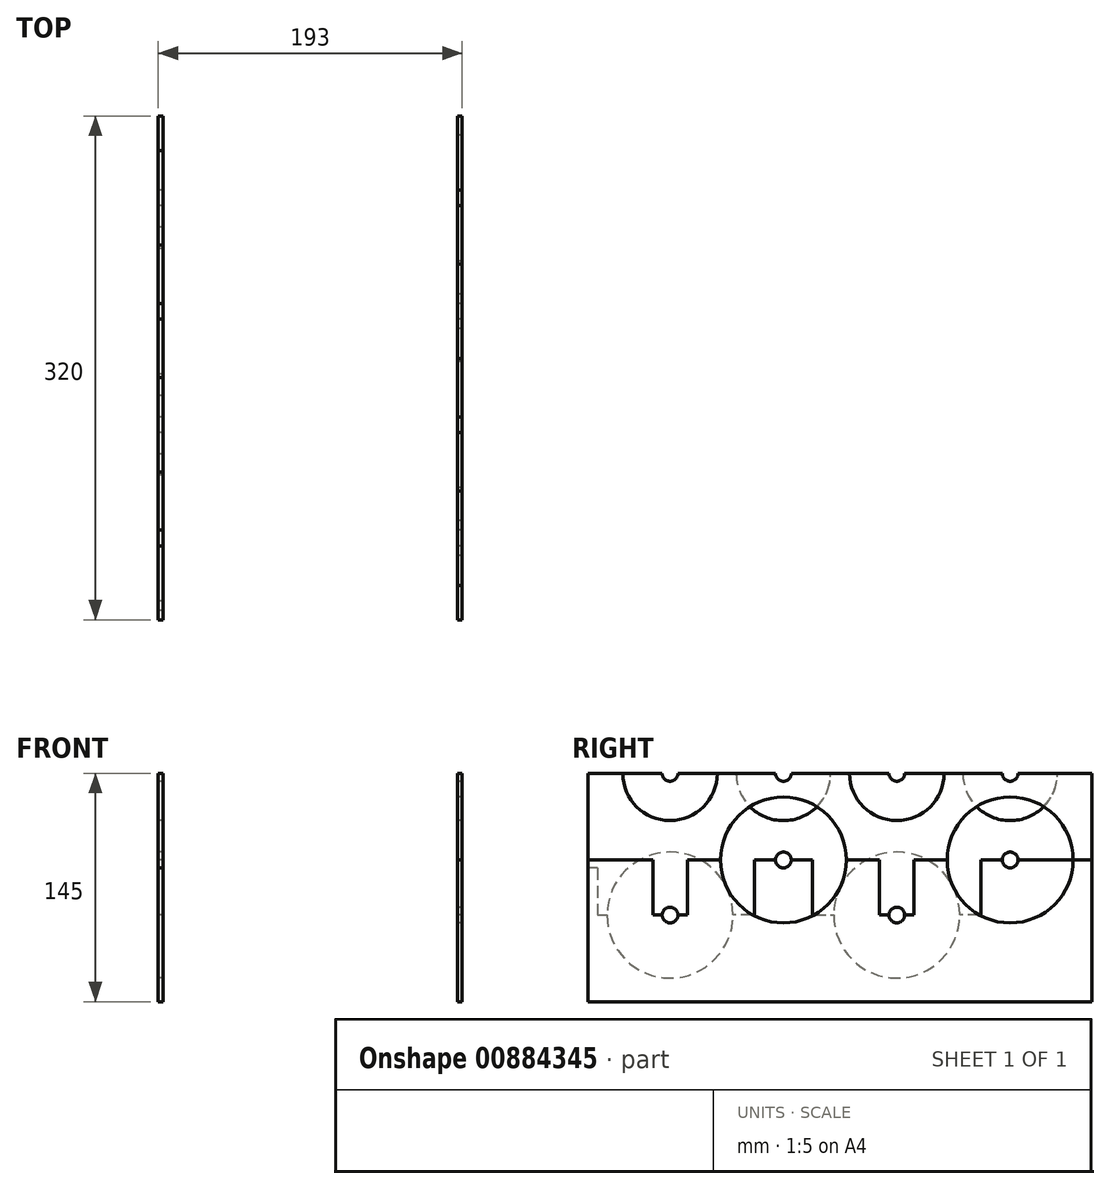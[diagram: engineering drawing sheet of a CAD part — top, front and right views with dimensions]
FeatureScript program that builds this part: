
annotation { "Feature Type Name" : "Feature", "Feature Type Description" : "" }
export const myFeature = defineFeature(function(context is Context, id is Id, definition is map)
    precondition{}
    {
        {
            var Q0;
            Q0=qCreatedBy(makeId("Right.planeOp"),FACE);
            var sketch = newSketch(context, id + "F0", { "sketchPlane" : qUnion([Q0])});
            skLineSegment(sketch, "E0.bottom", {"start": v(160, -42.5) * mm, "end": v(-160, -42.5) * mm});
            skLineSegment(sketch, "E0.right", {"start": v(-160, -42.5) * mm, "end": v(-160, 42.5) * mm});
            skPoint(sketch, "E0.middle", {"position": v(0, 0) * mm});
            skArc(sketch, "E1", {"start": v(-68, 12.5) * mm, "mid": v(-108, -27.5) * mm, "end": v(-148, 12.5) * mm});
            skArc(sketch, "E2", {"start": v(-4, 12.5) * mm, "mid": v(36, -27.5) * mm, "end": v(76, 12.5) * mm});
            skPoint(sketch, "E3", {"position": v(11.64, 12.5) * mm});
            skArc(sketch, "E4", {"start": v(113, 47.5) * mm, "mid": v(108, 42.5) * mm, "end": v(103, 47.5) * mm});
            skArc(sketch, "E5", {"start": v(-31, 47.5) * mm, "mid": v(-36, 42.5) * mm, "end": v(-41, 47.5) * mm});
            skLineSegment(sketch, "E6", {"start": v(-54.5, 47.5) * mm, "end": v(-41, 47.5) * mm});
            skLineSegment(sketch, "E7", {"start": v(89.5, 47.5) * mm, "end": v(103, 47.5) * mm});
            skLineSegment(sketch, "E8.trimOffspring", {"start": v(-31, 47.5) * mm, "end": v(-17.5, 47.5) * mm});
            skLineSegment(sketch, "E9.trimOffspring", {"start": v(113, 47.5) * mm, "end": v(160, 47.5) * mm});
            skLineSegment(sketch, "E10", {"start": v(160, -42.5) * mm, "end": v(160, 47.5) * mm});
            skLineSegment(sketch, "E11", {"start": v(-154, 42.5) * mm, "end": v(-160, 42.5) * mm});
            skLineSegment(sketch, "E12", {"start": v(-17.5, 47.5) * mm, "end": v(-17.5, 12.5) * mm});
            skLineSegment(sketch, "E13", {"start": v(-17.5, 12.5) * mm, "end": v(-4, 12.5) * mm});
            skLineSegment(sketch, "E14", {"start": v(89.5, 47.5) * mm, "end": v(89.5, 12.5) * mm});
            skLineSegment(sketch, "E15", {"start": v(89.5, 12.5) * mm, "end": v(76, 12.5) * mm});
            skLineSegment(sketch, "E16", {"start": v(-54.5, 47.5) * mm, "end": v(-54.5, 12.5) * mm});
            skLineSegment(sketch, "E17", {"start": v(-54.5, 12.5) * mm, "end": v(-68, 12.5) * mm});
            skPoint(sketch, "E18.end.orphan", {"position": v(-68, 47.5) * mm});
            skPoint(sketch, "E19.start.orphan", {"position": v(-4, 47.5) * mm});
            skPoint(sketch, "E20.orphan", {"position": v(76, 47.5) * mm});
            skLineSegment(sketch, "E21", {"start": v(-154, 42.5) * mm, "end": v(-154, 12.5) * mm});
            skLineSegment(sketch, "E22", {"start": v(-154, 12.5) * mm, "end": v(-148, 12.5) * mm});
            skPoint(sketch, "E23.end.orphan", {"position": v(-148, 42.5) * mm});
            skLineSegment(sketch, "E24", {"start": v(-160, 42.5) * mm, "end": v(-160, 102.5) * mm});
            skLineSegment(sketch, "E25", {"start": v(-160, 102.5) * mm, "end": v(-113, 102.5) * mm});
            skLineSegment(sketch, "E26", {"start": v(160, 102.5) * mm, "end": v(160, 47.5) * mm});
            skArc(sketch, "E27", {"start": v(103, 47.5) * mm, "mid": v(108, 52.5) * mm, "end": v(113, 47.5) * mm});
            skArc(sketch, "E28", {"start": v(-41, 47.5) * mm, "mid": v(-36, 52.5) * mm, "end": v(-31, 47.5) * mm});
            skArc(sketch, "E29", {"start": v(-4, 12.5) * mm, "mid": v(36, 52.5) * mm, "end": v(76, 12.5) * mm});
            skArc(sketch, "E30", {"start": v(-148, 12.5) * mm, "mid": v(-108, 52.5) * mm, "end": v(-68, 12.5) * mm});
            skArc(sketch, "E31", {"start": v(78, 102.5) * mm, "mid": v(108, 72.5) * mm, "end": v(138, 102.5) * mm});
            skArc(sketch, "E32", {"start": v(-66, 102.5) * mm, "mid": v(-36, 72.5) * mm, "end": v(-6, 102.5) * mm});
            skArc(sketch, "E33", {"start": v(-113, 102.5) * mm, "mid": v(-108, 97.5) * mm, "end": v(-103, 102.5) * mm});
            skArc(sketch, "E34", {"start": v(31, 102.5) * mm, "mid": v(36, 97.5) * mm, "end": v(41, 102.5) * mm});
            skLineSegment(sketch, "E35.trimOffspring", {"start": v(41, 102.5) * mm, "end": v(78, 102.5) * mm});
            skLineSegment(sketch, "E36.trimOffspring", {"start": v(-103, 102.5) * mm, "end": v(-66, 102.5) * mm});
            skLineSegment(sketch, "E37.trimOffspring", {"start": v(-6, 102.5) * mm, "end": v(31, 102.5) * mm});
            skLineSegment(sketch, "E38.trimOffspring", {"start": v(138, 102.5) * mm, "end": v(160, 102.5) * mm});
            skSolve(sketch);
        }
        {
            var Q0;
            Q0=makeQuery(id+"F0.imprint","IMPRINT",FACE,{"disambiguationData":[TD([[makeQuery(id+"F0.imprint","IMPRINT",EDGE,{"derivedFrom":sQuery(id+"F0.wireOp",EDGE,"E0.bottom")}),-1.0]])]});
            extrude(context, id + "F1", {"entities" : qUnion([Q0]), "depth" : 3 * mm, "offsetDistance" : 25 * mm});
        }
        {
            var Q0;
            Q0=makeQuery(id+"F0.imprint","IMPRINT",FACE,{"disambiguationData":[TD([[makeQuery(id+"F0.imprint","IMPRINT",EDGE,{"derivedFrom":sQuery(id+"F0.wireOp",EDGE,"E6")}),1.0]])]});
            extrude(context, id + "F2", {"entities" : qUnion([Q0]), "depth" : 3 * mm, "offsetDistance" : 25 * mm});
        }
        {
            var Q0;
            Q0=qCreatedBy(makeId("Right.planeOp"),FACE);
            cPlane(context, id + "F3", {"entities" : qUnion([Q0]), "cplaneType" : CPlaneType.OFFSET, "offset" : 190 * mm, "width" : 150 * mm, "height" : 150 * mm});
        }
        {
            var Q0;
            Q0=qCreatedBy(id+"F3.planeOp",FACE);
            var sketch = newSketch(context, id + "F4", { "sketchPlane" : qUnion([Q0])});
            skLineSegment(sketch, "E39.bottom", {"start": v(160, -42.5) * mm, "end": v(-160, -42.5) * mm});
            skLineSegment(sketch, "E39.right", {"start": v(-160, -42.5) * mm, "end": v(-160, 47.5) * mm});
            skPoint(sketch, "E39.middle", {"position": v(0, 2.5) * mm});
            skArc(sketch, "E40", {"start": v(31, 12.5) * mm, "mid": v(36, 7.5) * mm, "end": v(41, 12.5) * mm});
            skArc(sketch, "E41", {"start": v(148, 47.5) * mm, "mid": v(108, 7.5) * mm, "end": v(68, 47.5) * mm});
            skArc(sketch, "E42", {"start": v(4, 47.5) * mm, "mid": v(-36, 7.5) * mm, "end": v(-76, 47.5) * mm});
            skLineSegment(sketch, "E43", {"start": v(-97, 47.5) * mm, "end": v(-76, 47.5) * mm});
            skLineSegment(sketch, "E44", {"start": v(47, 47.5) * mm, "end": v(68, 47.5) * mm});
            skLineSegment(sketch, "E45.trimOffspring", {"start": v(4, 47.5) * mm, "end": v(25, 47.5) * mm});
            skLineSegment(sketch, "E46.trimOffspring", {"start": v(148, 47.5) * mm, "end": v(160, 47.5) * mm});
            skLineSegment(sketch, "E47", {"start": v(160, -42.5) * mm, "end": v(160, 47.5) * mm});
            skLineSegment(sketch, "E48", {"start": v(-119, 47.5) * mm, "end": v(-160, 47.5) * mm});
            skLineSegment(sketch, "E49", {"start": v(25, 47.5) * mm, "end": v(25, 12.5) * mm});
            skLineSegment(sketch, "E50", {"start": v(25, 12.5) * mm, "end": v(31, 12.5) * mm});
            skLineSegment(sketch, "E51", {"start": v(47, 47.5) * mm, "end": v(47, 12.5) * mm});
            skLineSegment(sketch, "E52", {"start": v(47, 12.5) * mm, "end": v(41, 12.5) * mm});
            skLineSegment(sketch, "E53", {"start": v(-97, 47.5) * mm, "end": v(-97, 12.5) * mm});
            skLineSegment(sketch, "E54", {"start": v(-97, 12.5) * mm, "end": v(-103, 12.5) * mm});
            skLineSegment(sketch, "E55", {"start": v(-119, 47.5) * mm, "end": v(-119, 12.5) * mm});
            skLineSegment(sketch, "E56", {"start": v(-119, 12.5) * mm, "end": v(-113, 12.5) * mm});
            skLineSegment(sketch, "E57", {"start": v(-160, 47.5) * mm, "end": v(-160, 102.5) * mm});
            skLineSegment(sketch, "E58", {"start": v(-160, 102.5) * mm, "end": v(-138, 102.5) * mm});
            skLineSegment(sketch, "E59", {"start": v(160, 102.5) * mm, "end": v(160, 47.5) * mm});
            skArc(sketch, "E60", {"start": v(-113, 12.5) * mm, "mid": v(-108, 7.5) * mm, "end": v(-103, 12.5) * mm});
            skArc(sketch, "E61", {"start": v(103, 102.5) * mm, "mid": v(108, 97.5) * mm, "end": v(113, 102.5) * mm});
            skArc(sketch, "E62", {"start": v(-41, 102.5) * mm, "mid": v(-36, 97.5) * mm, "end": v(-31, 102.5) * mm});
            skArc(sketch, "E63", {"start": v(-138, 102.5) * mm, "mid": v(-108, 72.5) * mm, "end": v(-78, 102.5) * mm});
            skArc(sketch, "E64", {"start": v(6, 102.5) * mm, "mid": v(36, 72.5) * mm, "end": v(66, 102.5) * mm});
            skLineSegment(sketch, "E65.trimOffspring", {"start": v(66, 102.5) * mm, "end": v(103, 102.5) * mm});
            skLineSegment(sketch, "E66.trimOffspring", {"start": v(-78, 102.5) * mm, "end": v(-41, 102.5) * mm});
            skLineSegment(sketch, "E67.trimOffspring", {"start": v(-31, 102.5) * mm, "end": v(6, 102.5) * mm});
            skLineSegment(sketch, "E68.trimOffspring", {"start": v(113, 102.5) * mm, "end": v(160, 102.5) * mm});
            skArc(sketch, "E69", {"start": v(-113, 12.5) * mm, "mid": v(-108, 17.5) * mm, "end": v(-103, 12.5) * mm});
            skArc(sketch, "E70", {"start": v(-76, 47.5) * mm, "mid": v(-36, 87.5) * mm, "end": v(4, 47.5) * mm});
            skArc(sketch, "E71", {"start": v(31, 12.5) * mm, "mid": v(36, 17.5) * mm, "end": v(41, 12.5) * mm});
            skArc(sketch, "E72", {"start": v(68, 47.5) * mm, "mid": v(108, 87.5) * mm, "end": v(148, 47.5) * mm});
            skSolve(sketch);
        }
        {
            var Q0;
            Q0=makeQuery(id+"F4.imprint","IMPRINT",FACE,{"disambiguationData":[TD([[makeQuery(id+"F4.imprint","IMPRINT",EDGE,{"derivedFrom":sQuery(id+"F4.wireOp",EDGE,"E39.bottom")}),-1.0]])]});
            extrude(context, id + "F5", {"entities" : qUnion([Q0]), "depth" : 3 * mm, "offsetDistance" : 25 * mm});
        }
        {
            var Q0;
            Q0=makeQuery(id+"F4.imprint","IMPRINT",FACE,{"disambiguationData":[TD([[makeQuery(id+"F4.imprint","IMPRINT",EDGE,{"derivedFrom":sQuery(id+"F4.wireOp",EDGE,"E43")}),1.0]])]});
            extrude(context, id + "F6", {"entities" : qUnion([Q0]), "depth" : 3 * mm, "offsetDistance" : 25 * mm});
        }
    });
